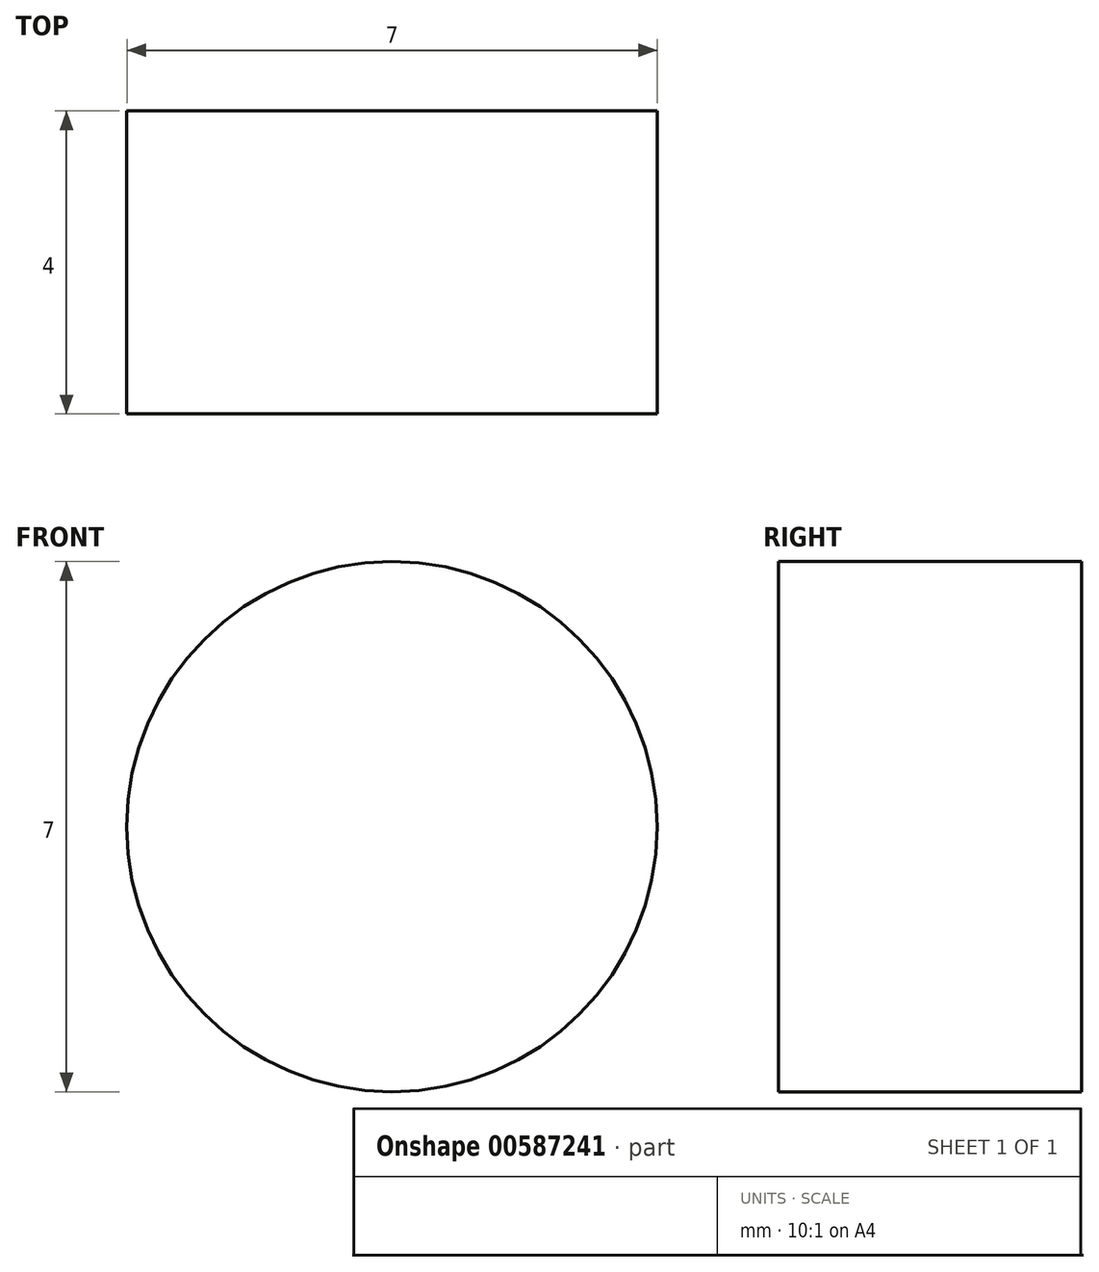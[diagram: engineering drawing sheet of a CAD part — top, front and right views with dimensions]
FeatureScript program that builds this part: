
annotation { "Feature Type Name" : "Feature", "Feature Type Description" : "" }
export const myFeature = defineFeature(function(context is Context, id is Id, definition is map)
    precondition{}
    {
        {
            var Q0;
            Q0=qCreatedBy(makeId("Front.planeOp"),FACE);
            var sketch = newSketch(context, id + "F0", { "sketchPlane" : qUnion([Q0])});
            skCircle(sketch, "E0", {"center": v(-7.31, 3.93) * mm, "radius": 3.5 * mm});
            skSolve(sketch);
        }
        {
            var Q0;
            Q0=makeQuery(id+"F0.imprint","IMPRINT",FACE,{"disambiguationData":[TD([[makeQuery(id+"F0.imprint","IMPRINT",EDGE,{"derivedFrom":sQuery(id+"F0.wireOp",EDGE,"E0")}),1.0]])]});
            extrude(context, id + "F1", {"entities" : qUnion([Q0]), "depth" : 4 * mm, "offsetDistance" : 25 * mm});
        }
    });
